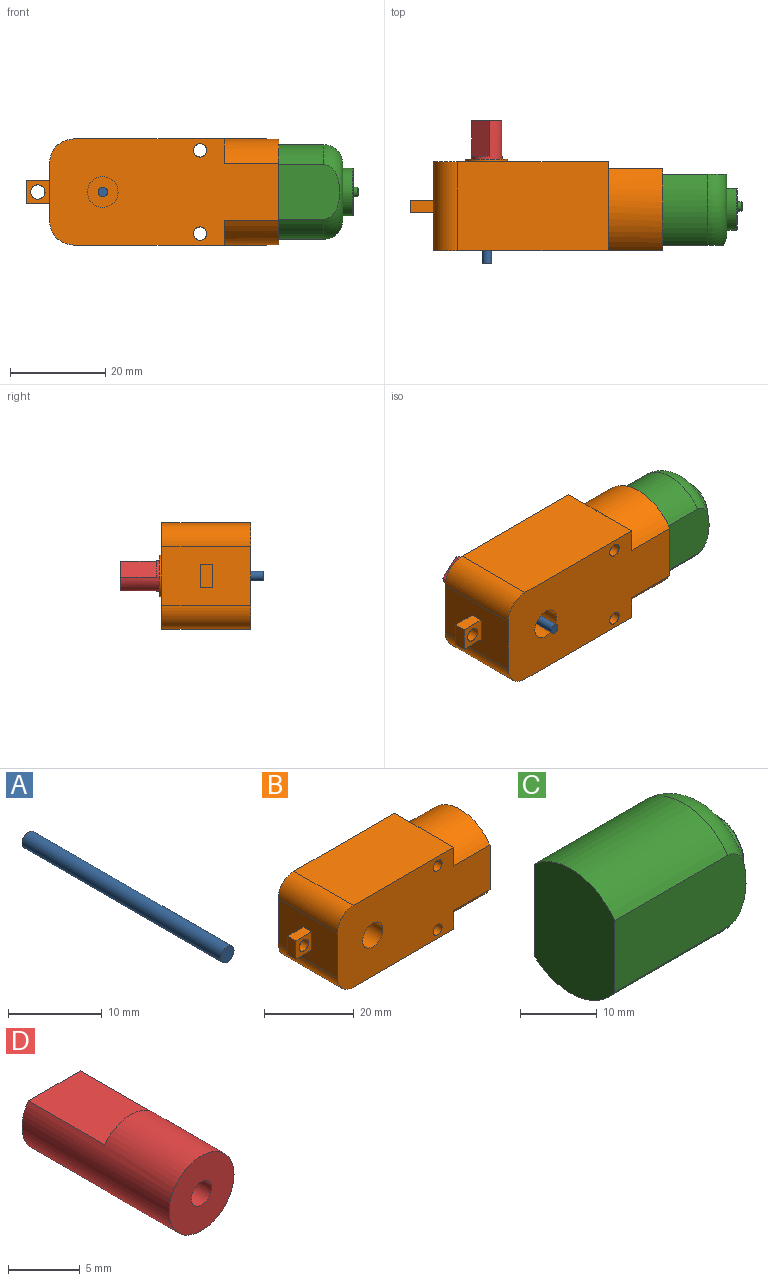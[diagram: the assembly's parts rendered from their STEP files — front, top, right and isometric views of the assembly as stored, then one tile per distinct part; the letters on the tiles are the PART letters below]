
ASSEMBLY  parts=4 mates=3
PART A: 3 faces, bbox 2x30x2 mm
  f0: cylinder r=1mm len=30mm, axis (0,1,0), area 188.5mm2, adj f1,f2
  f1: plane 2x2mm, normal (0,-1,0), area 3.1mm2, adj f0
  f2: plane 2x2mm, normal (0,1,0), area 3.1mm2, adj f0
PART B: 34 faces, bbox 53.1x19.2x22.3 mm
  f0: cylinder r=3.2mm len=6.85mm, axis (0,1,0), area 137.7mm2, adj f31,f33
  f1: plane 9.35x5.08mm, normal (1,0,0), area 14mm2, adj f5,f12,f25
  f2: plane 22.3x9.35mm, normal (1,0,0), area 47.7mm2, adj f5,f8,f13,f23,f24,f25
  f3: plane 9.35x5.08mm, normal (1,0,0), area 14mm2, adj f8,f12,f23
  f4: plane 18.7x12.3mm, normal (-1,0,0), area 217mm2, adj f6,f7,f12,f13,f14,f15,f16,f17
  f5: plane 31.7x18.7mm, normal (0,0,1), area 592.8mm2, adj f1,f2,f6,f12,f13
  f6: cylinder r=5mm len=18.7mm, axis (0,1,0), area 146.9mm2, adj f4,f5,f12,f13
  f7: cylinder r=5mm len=18.7mm, axis (0,1,0), area 146.9mm2, adj f4,f8,f12,f13
  f8: plane 31.7x18.7mm, normal (0,0,-1), area 592.8mm2, adj f2,f3,f7,f12,f13
  f9: cylinder r=1.4mm len=18.7mm, axis (0,1,0), area 164.5mm2, adj f12,f13
  f10: cylinder r=3.2mm len=6.4mm, axis (0,1,0), area 127.7mm2, adj f12,f30
  f11: cylinder r=1.4mm len=18.7mm, axis (0,1,0), area 164.5mm2, adj f12,f13
  f12: plane 48.1x22.3mm, normal (0,-1,0), area 901.7mm2, adj f1,f3,f4,f5,f6,f7,f8,f9
  f13: plane 36.7x22.3mm, normal (0,1,0), area 734.5mm2, adj f2,f4,f5,f6,f7,f8,f9,f11
  f14: plane 5x5mm, normal (0,-1,0), area 17.9mm2, adj f4,f15,f17,f18,f19
  f15: plane 5x2.6mm, normal (0,0,1), area 13mm2, adj f4,f14,f16,f18
  f16: plane 5x5mm, normal (0,1,0), area 17.9mm2, adj f4,f15,f17,f18,f19
  f17: plane 5x2.6mm, normal (0,0,-1), area 13mm2, adj f4,f14,f16,f18
  f18: plane 5x2.6mm, normal (-1,0,0), area 13mm2, adj f14,f15,f16,f17
  f19: cylinder r=1.5mm len=3mm, axis (0,-1,0), area 24.5mm2, adj f14,f16
  f20: cylinder r=9.95mm len=14.9mm, axis (-1,0,0), area 193.4mm2, adj f21,f26,f27,f28
  f21: plane 14.62x11.4mm, normal (0,-1,0), area 166.7mm2, adj f20,f22,f27,f28
  f22: cylinder r=9.95mm len=14.9mm, axis (-1,0,0), area 193.4mm2, adj f21,f26,f27,f28
  f23: cylinder r=11.15mm len=17.3mm, axis (-1,0,0), area 227.3mm2, adj f2,f3,f12,f24,f27
  f24: plane 15.64x11.4mm, normal (0,1,0), area 178.2mm2, adj f2,f23,f25,f27
  f25: cylinder r=11.15mm len=17.3mm, axis (-1,0,0), area 227.3mm2, adj f1,f2,f12,f24,f27
  f26: plane 11.42x11.4mm, normal (0,1,0), area 130.1mm2, adj f20,f22,f27,f28
  f27: plane 22.3x17.3mm, normal (1,0,0), area 76.6mm2, adj f12,f20,f21,f22,f23,f24,f25,f26
  f28: plane 19.9x14.9mm, normal (1,0,0), area 264.7mm2, adj f20,f21,f22,f26
  f29: cylinder r=1mm len=6mm, axis (0,1,0), area 37.7mm2, adj f30,f31
  f30: plane 6.4x6.4mm, normal (0,-1,0), area 29mm2, adj f10,f29
  f31: plane 6.4x6.4mm, normal (0,1,0), area 29mm2, adj f0,f29
  f32: cylinder r=4.4mm len=8.8mm, axis (0,-1,0), area 13.8mm2, adj f13,f33
  f33: plane 8.8x8.8mm, normal (0,1,0), area 28.7mm2, adj f0,f32
PART C: 14 faces, bbox 28.2x21.6x21.6 mm
  f0: plane 11.9x11.9mm, normal (1,0,0), area 38.3mm2, adj f6,f7,f8
  f1: plane 24.82x14.62mm, normal (0,1,0), area 353.1mm2, adj f2,f4,f5,f6
  f2: cylinder r=9.95mm len=20.9mm, axis (-1,0,0), area 354.6mm2, adj f1,f3,f5,f6
  f3: plane 24.24x11.42mm, normal (0,-1,0), area 269.2mm2, adj f2,f4,f5,f6
  f4: cylinder r=9.95mm len=20.9mm, axis (-1,0,0), area 354.6mm2, adj f1,f3,f5,f6
  f5: plane 19.9x14.9mm, normal (-1,0,0), area 264.7mm2, adj f1,f2,f3,f4
  f6: torus R=5.95mm, axis (-1,0,0), area 233.4mm2, adj f0,f1,f2,f3,f4
  f7: plane 6.7x2.29mm, normal (0,1,0), area 14.5mm2, adj f0,f8,f9,f13
  f8: cylinder r=5mm len=10mm, axis (-1,0,0), area 48.4mm2, adj f0,f7,f13
  f9: plane 9.6x8.55mm, normal (1,0,0), area 64.9mm2, adj f7,f10,f13
  f10: cylinder r=1mm len=2mm, axis (-1,0,0), area 5mm2, adj f9,f12
  f11: plane 1.6x1.6mm, normal (1,0,0), area 2mm2, adj f12
  f12: torus R=0.8mm, axis (1,0,0), area 1.8mm2, adj f10,f11
  f13: torus R=4.8mm, axis (1,0,0), area 7.6mm2, adj f7,f8,f9
PART D: 8 faces, bbox 6.4x14.5x6.4 mm
  f0: cylinder r=3.2mm len=14.5mm, axis (0,-1,0), area 202.5mm2, adj f2,f3,f4,f5,f6,f7
  f1: cylinder r=1mm len=14.5mm, axis (0,-1,0), area 91.1mm2, adj f2,f3
  f2: plane 6.4x3.84mm, normal (0,1,0), area 19.9mm2, adj f0,f1,f4,f6
  f3: plane 6.4x6.4mm, normal (0,-1,0), area 29mm2, adj f0,f1
  f4: plane 7.5x5.12mm, normal (0,0,-1), area 38.4mm2, adj f0,f2,f5
  f5: plane 5.12x1.28mm, normal (0,1,0), area 4.6mm2, adj f0,f4
  f6: plane 7.5x5.12mm, normal (0,0,1), area 38.4mm2, adj f0,f2,f7
  f7: plane 5.12x1.28mm, normal (0,1,0), area 4.6mm2, adj f0,f6
PLACE A rot(axis=(0,-1,0),42.2deg) t=(-23.72,12.87,-1.64)mm
PLACE B t=(-21.85,9.87,-6.48)mm fixed
PLACE C t=(-21.85,9.87,-6.48)mm
PLACE D rot(axis=(0,-1,0),42.2deg) t=(-23.72,10.37,-1.64)mm
MATE fastened A.f0 <-> D.f0  axis (0,1,0) through (-29.05,27.87,-6.48)mm
MATE fastened B.f28 <-> C.f5  axis (1,0,0) through (-3.5,9.36,-6.48)mm
MATE revolute A.f0 <-> B.f0  axis (0,1,0) through (-29.05,12.87,-6.48)mm
